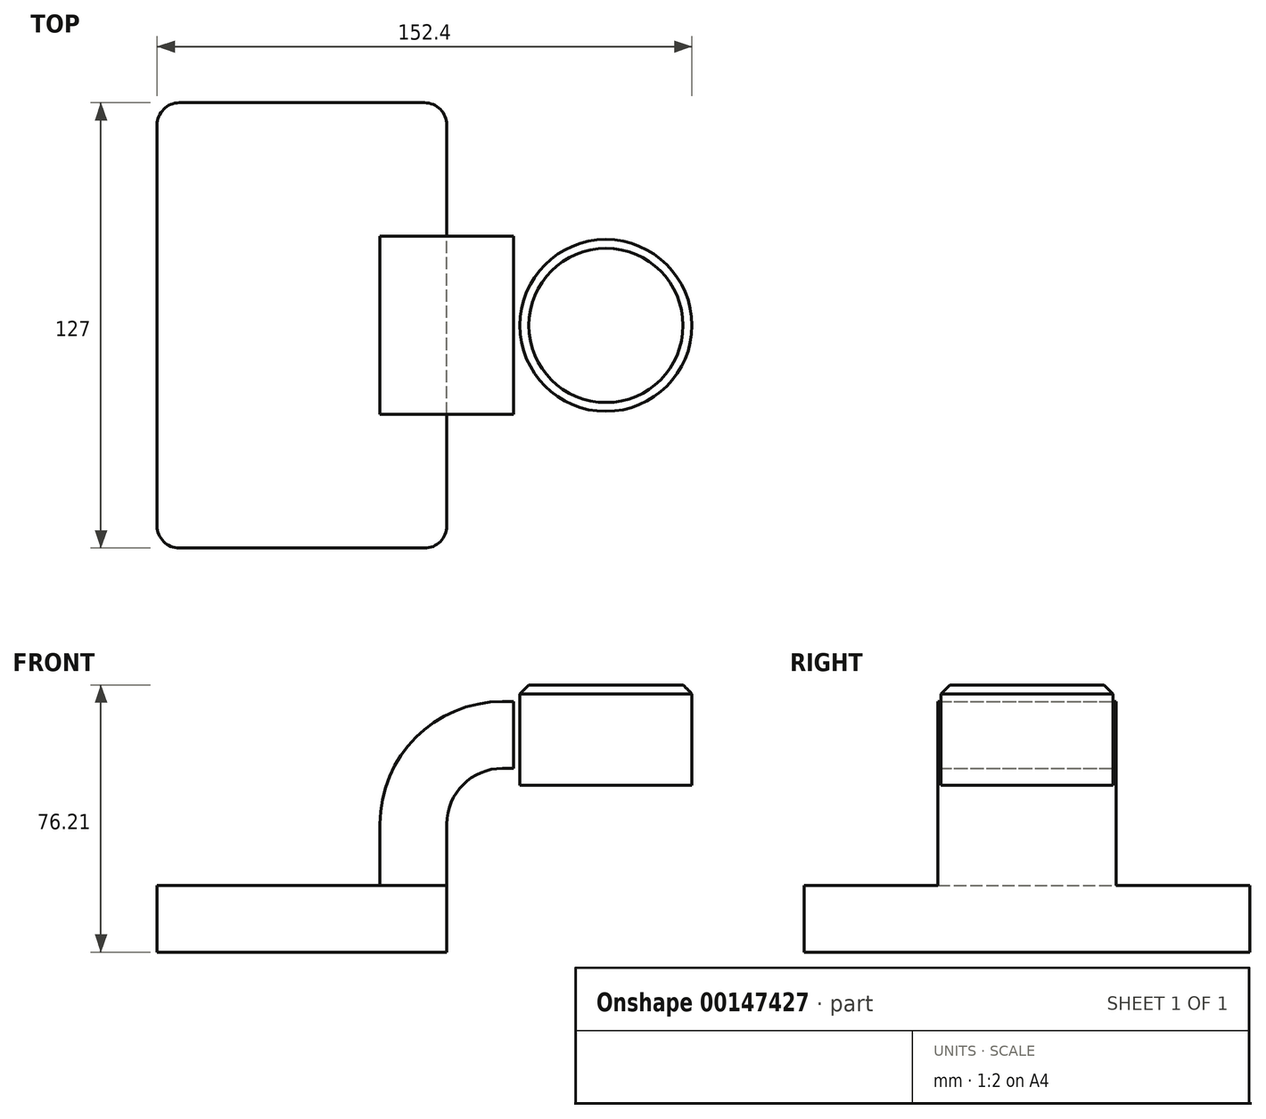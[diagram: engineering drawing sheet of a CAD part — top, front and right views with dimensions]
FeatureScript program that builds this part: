
annotation { "Feature Type Name" : "Feature", "Feature Type Description" : "" }
export const myFeature = defineFeature(function(context is Context, id is Id, definition is map)
    precondition{}
    {
        {
            var Q0;
            Q0=qCreatedBy(makeId("Front.planeOp"),FACE);
            var sketch = newSketch(context, id + "F0", { "sketchPlane" : qUnion([Q0])});
            skLineSegment(sketch, "E0.bottom", {"start": v(-41.28, 9.52) * mm, "end": v(41.27, 9.53) * mm});
            skLineSegment(sketch, "E0.top", {"start": v(-41.28, -9.53) * mm, "end": v(41.28, -9.53) * mm});
            skLineSegment(sketch, "E0.left", {"start": v(-41.28, 9.52) * mm, "end": v(-41.28, -9.53) * mm});
            skLineSegment(sketch, "E0.right", {"start": v(41.27, 9.53) * mm, "end": v(41.28, -9.52) * mm});
            skPoint(sketch, "E0.middle", {"position": v(0, 0) * mm});
            skLineSegment(sketch, "E1.bottom", {"start": v(60.32, 38.1) * mm, "end": v(111.12, 38.1) * mm});
            skLineSegment(sketch, "E1.top", {"start": v(60.32, 66.67) * mm, "end": v(111.12, 66.67) * mm});
            skLineSegment(sketch, "E1.left", {"start": v(60.32, 38.1) * mm, "end": v(60.32, 66.67) * mm});
            skLineSegment(sketch, "E1.right", {"start": v(111.12, 38.1) * mm, "end": v(111.12, 66.67) * mm});
            skPoint(sketch, "E1.middle", {"position": v(85.72, 52.39) * mm});
            skLineSegment(sketch, "E2", {"start": v(41.27, 9.53) * mm, "end": v(41.27, 27) * mm});
            skArc(sketch, "E3", {"start": v(41.27, 27) * mm, "mid": v(45.92, 38.23) * mm, "end": v(57.15, 42.88) * mm});
            skLineSegment(sketch, "E4", {"start": v(57.15, 42.88) * mm, "end": v(86.61, 42.88) * mm});
            skLineSegment(sketch, "E5", {"start": v(86.61, 42.88) * mm, "end": v(76.24, 42.88) * mm});
            skLineSegment(sketch, "E6.0", {"start": v(57.15, 61.93) * mm, "end": v(86.61, 61.93) * mm});
            skArc(sketch, "E6.1", {"start": v(22.22, 27) * mm, "mid": v(32.45, 51.7) * mm, "end": v(57.15, 61.93) * mm});
            skLineSegment(sketch, "E6.2", {"start": v(22.22, 9.53) * mm, "end": v(22.22, 27) * mm});
            skLineSegment(sketch, "E7", {"start": v(86.61, 66.67) * mm, "end": v(86.61, 38.1) * mm});
            skFitSpline(sketch, "E8", {"points": [v(-41.28, 9.52) * mm, v(57.15, 61.93) * mm], "startDerivative": vector(0.23, 70.79) * mm, "endDerivative": vector(118.88, -9.89) * mm});
            skSolve(sketch);
        }
        {
            var Q0;
            Q0=makeQuery(id+"F0.imprint","IMPRINT",FACE,{"disambiguationData":[TD([[makeQuery(id+"F0.imprint","IMPRINT",EDGE,{"derivedFrom":sQuery(id+"F0.wireOp",EDGE,"E0.top")}),1.0]])]});
            extrude(context, id + "F1", {"entities" : qUnion([Q0]), "endBound" : BoundingType.SYMMETRIC, "depth" : 127 * mm});
        }
        {
            var Q0;
            {var subQ5=sQuery(id+"F0.wireOp",EDGE,"E2");Q0=makeQuery(id+"F0.imprint","IMPRINT",FACE,{"disambiguationData":[TD([[makeQuery(id+"F0.imprint","IMPRINT",EDGE,{"derivedFrom":subQ5}),1.0]])]});}
            var Q1;
            {var subQ5=sQuery(id+"F0.wireOp",EDGE,"E5");Q1=makeQuery(id+"F0.imprint","IMPRINT",FACE,{"disambiguationData":[TD([[makeQuery(id+"F0.imprint","IMPRINT",EDGE,{"derivedFrom":subQ5}),-1.0]])]});}
            extrude(context, id + "F2", {"entities" : qUnion([Q0, Q1]), "operationType" : NewBodyOperationType.ADD, "endBound" : BoundingType.SYMMETRIC, "depth" : 50.8 * mm});
        }
        {
            var Q0;
            Q0=makeQuery(id+"F0.imprint","IMPRINT",FACE,{"disambiguationData":[TD([[makeQuery(id+"F0.imprint","IMPRINT",EDGE,{"derivedFrom":sQuery(id+"F0.wireOp",EDGE,"E6.1")}),1.0]])]});
            extrude(context, id + "F3", {"entities" : qUnion([Q0]), "operationType" : NewBodyOperationType.ADD, "endBound" : BoundingType.SYMMETRIC, "depth" : 15.88 * mm});
        }
        {
            var Q0;
            {var subQ0=sQuery(id+"F0.wireOp",EDGE,"E1.right");Q0=makeQuery(id+"F0.imprint","IMPRINT",FACE,{"disambiguationData":[TD([[makeQuery(id+"F0.imprint","IMPRINT",EDGE,{"derivedFrom":subQ0}),1.0]])]});}
            var Q1;
            Q1=sQuery(id+"F0.wireOp",EDGE,"E7");
            revolve(context, id + "F4", {"operationType" : NewBodyOperationType.ADD, "entities" : qUnion([Q0]), "axis" : qUnion([Q1]), "revolveType" : RevolveType.FULL});
        }
        {
            var Q0;
            Q0=makeQuery(id+"F1.opExtrude","CAP_EDGE",EDGE,{"disambiguationData":[OSD([sQuery(id+"F0.wireOp",EDGE,"E0.left")])],"isStart":false});
            var Q1;
            Q1=makeQuery(id+"F1.opExtrude","CAP_EDGE",EDGE,{"disambiguationData":[OSD([sQuery(id+"F0.wireOp",EDGE,"E0.right")])],"isStart":false});
            var Q2;
            Q2=makeQuery(id+"F1.opExtrude","CAP_EDGE",EDGE,{"disambiguationData":[OSD([sQuery(id+"F0.wireOp",EDGE,"E0.right")])],"isStart":true});
            var Q3;
            Q3=makeQuery(id+"F1.opExtrude","CAP_EDGE",EDGE,{"disambiguationData":[OSD([sQuery(id+"F0.wireOp",EDGE,"E0.left")])],"isStart":true});
            fillet(context, id + "F5", {"entities" : qUnion([Q0, Q1, Q2, Q3]), "radius" : 6.35 * mm, "tangentPropagation" : true, "allowEdgeOverflow" : false});
        }
        {
            var Q0;
            Q0=makeQuery(id+"F4.opRevolve","SWEPT_EDGE",EDGE,{"disambiguationData":[OSD([sQuery(id+"F0.wireOp",EDGE,"E1.top"),sQuery(id+"F0.wireOp",EDGE,"E1.right")])]});
            chamfer(context, id + "F6", {"entities" : qUnion([Q0]), "width" : 2.54 * mm, "tangentPropagation" : true});
        }
    });
